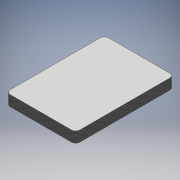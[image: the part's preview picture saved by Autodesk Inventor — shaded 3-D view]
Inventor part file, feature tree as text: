
AUTODESK INVENTOR PART (.ipt)
format: ipt  version: 2018 (Build 220112000, 112)  size: 305,664 bytes
history: native  units: mm
features: extrude x1, pattern_linear x1, sketch x1
ambient origin geometry x8: Origin, YZ Plane, XZ Plane, XY Plane, X Axis, Y Axis, Z Axis, Center Point
bodies: Solid1 (feature_tree)
feature tree (3):
  extrude  "Extrusion1"  Depth=89.0mm
  pattern_linear  "Rectangular Pattern1"  Spacing1=4.0mm  [1 undecoded]
  sketch  "Sketch1"  dims[d0=63.0mm d1=89.0mm d2=4.0mm d3=0.27mm d4=0.0mm d5=350.0mm d7=9.33mm]
note: 1 required parameter value undecoded (feature->parameter linkage not recoverable at this tier; creation-order binding heuristic only, values carry confidence <= 0.55)
